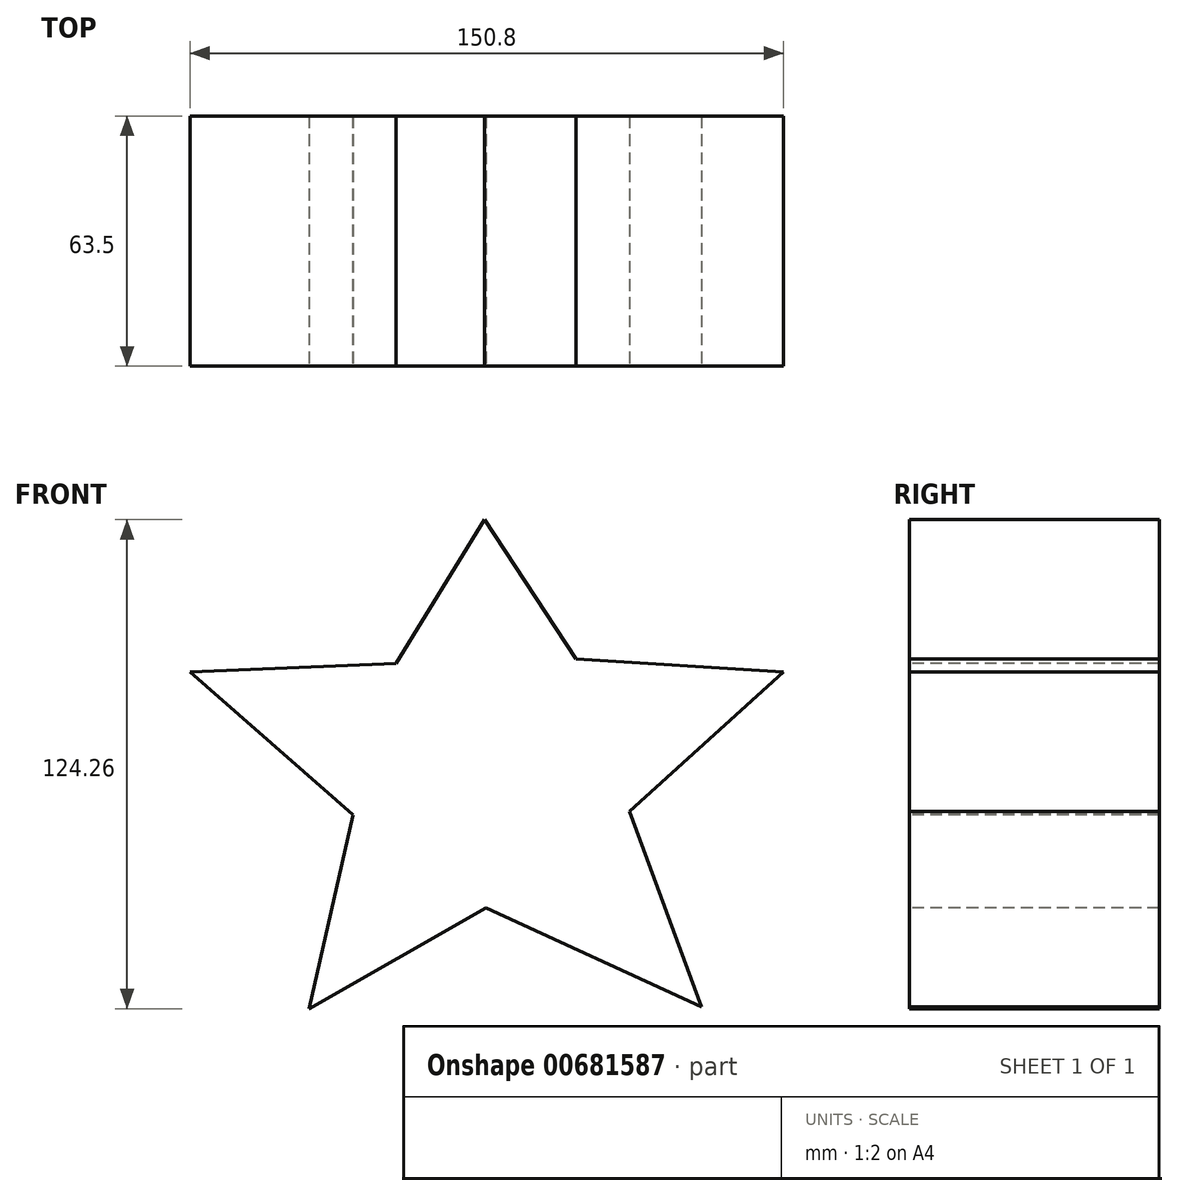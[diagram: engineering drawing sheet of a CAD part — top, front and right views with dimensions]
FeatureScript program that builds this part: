
annotation { "Feature Type Name" : "Feature", "Feature Type Description" : "" }
export const myFeature = defineFeature(function(context is Context, id is Id, definition is map)
    precondition{}
    {
        {
            var Q0;
            Q0=qCreatedBy(makeId("Front.planeOp"),FACE);
            var sketch = newSketch(context, id + "F0", { "sketchPlane" : qUnion([Q0])});
            skLineSegment(sketch, "E0", {"start": v(-22.5, 49.54) * mm, "end": v(0, 86.05) * mm});
            skLineSegment(sketch, "E1", {"start": v(0, 86.05) * mm, "end": v(23.22, 50.65) * mm});
            skLineSegment(sketch, "E2", {"start": v(23.22, 50.65) * mm, "end": v(75.95, 47.33) * mm});
            skLineSegment(sketch, "E3", {"start": v(75.95, 47.33) * mm, "end": v(36.87, 11.94) * mm});
            skLineSegment(sketch, "E4", {"start": v(36.87, 11.94) * mm, "end": v(55.3, -38.2) * mm});
            skLineSegment(sketch, "E5", {"start": v(55.3, -37.84) * mm, "end": v(0, -12.4) * mm});
            skLineSegment(sketch, "E6", {"start": v(0.73, -12.4) * mm, "end": v(-44.62, -38.2) * mm});
            skLineSegment(sketch, "E7", {"start": v(-44.62, -38.2) * mm, "end": v(-33.19, 11.94) * mm});
            skLineSegment(sketch, "E8", {"start": v(-33.56, 11.2) * mm, "end": v(-74.85, 47.33) * mm});
            skLineSegment(sketch, "E9", {"start": v(-74.85, 47.33) * mm, "end": v(-22.5, 49.54) * mm});
            skLineSegment(sketch, "E10", {"start": v(-33.56, 11.2) * mm, "end": v(-33.4, 11) * mm});
            skSolve(sketch);
        }
        {
            var Q0;
            Q0=makeQuery(id+"F0.imprint","IMPRINT",FACE,{"disambiguationData":[TD([[makeQuery(id+"F0.imprint","IMPRINT",EDGE,{"derivedFrom":sQuery(id+"F0.wireOp",EDGE,"E0")}),-1.0]])]});
            extrude(context, id + "F1", {"entities" : qUnion([Q0]), "oppositeDirection" : true, "depth" : 63.5 * mm, "offsetDistance" : 25.4 * mm});
        }
    });
